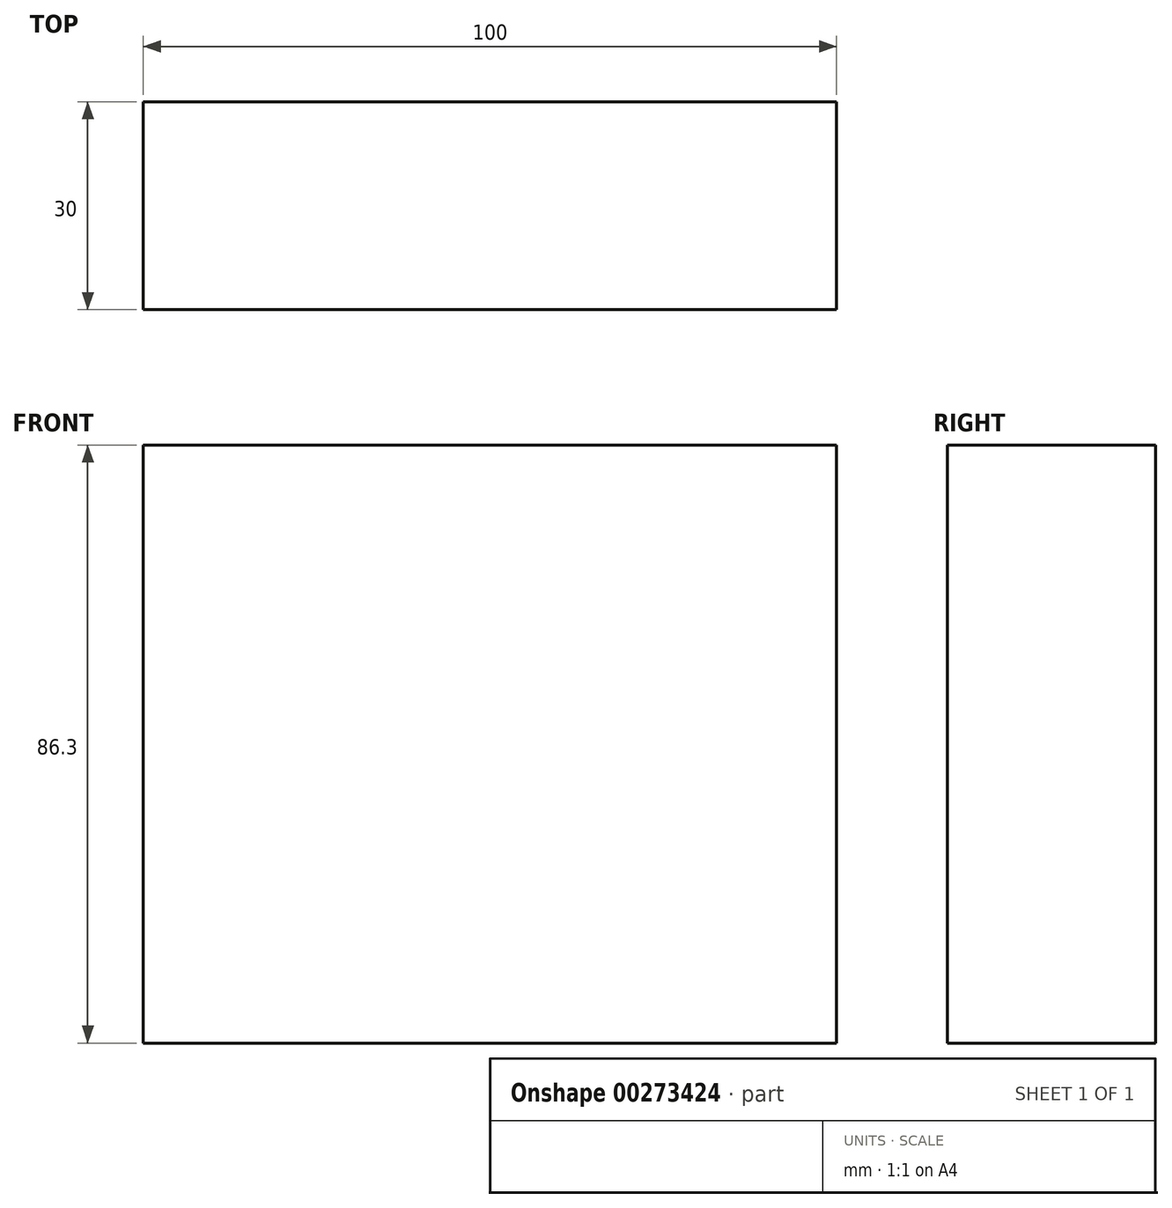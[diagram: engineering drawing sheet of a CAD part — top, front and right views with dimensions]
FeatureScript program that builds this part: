
annotation { "Feature Type Name" : "Feature", "Feature Type Description" : "" }
export const myFeature = defineFeature(function(context is Context, id is Id, definition is map)
    precondition{}
    {
        {
            var Q0;
            Q0=qCreatedBy(makeId("Front.planeOp"),FACE);
            var sketch = newSketch(context, id + "F0", { "sketchPlane" : qUnion([Q0])});
            skLineSegment(sketch, "E0.bottom", {"start": v(-50.1, 43.99) * mm, "end": v(49.9, 43.99) * mm});
            skLineSegment(sketch, "E0.top", {"start": v(-50.1, -42.3) * mm, "end": v(49.9, -42.3) * mm});
            skLineSegment(sketch, "E0.left", {"start": v(-50.1, 43.99) * mm, "end": v(-50.1, -42.3) * mm});
            skLineSegment(sketch, "E0.right", {"start": v(49.9, 43.99) * mm, "end": v(49.9, -42.3) * mm});
            skSolve(sketch);
        }
        {
            var Q0;
            Q0=makeQuery(id+"F0.imprint","IMPRINT",FACE,{"disambiguationData":[TD([[makeQuery(id+"F0.imprint","IMPRINT",EDGE,{"derivedFrom":sQuery(id+"F0.wireOp",EDGE,"E0.bottom")}),-1.0]])]});
            extrude(context, id + "F1", {"entities" : qUnion([Q0]), "depth" : 30 * mm});
        }
    });
